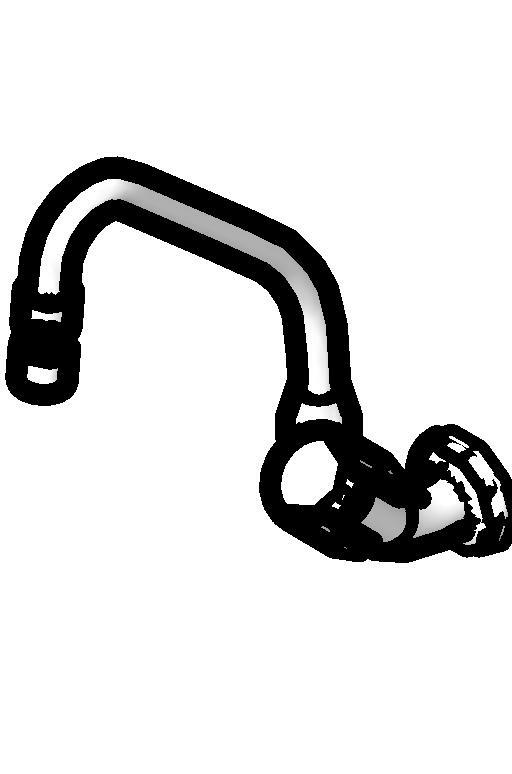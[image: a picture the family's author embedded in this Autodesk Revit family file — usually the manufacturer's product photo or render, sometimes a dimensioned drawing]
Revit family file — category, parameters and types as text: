
# Revit family: Deca_Torneira de parede para cozinha_Targa_1168.40
name_source: partatom
category: Plumbing Fixtures
units: mm (PartAtom-declared; Revit-internal decimal feet)

## family parameters
Cut with Voids When Loaded = No
Host = Face
Part Type = Normal
Room Calculation Point = No
Round Connector Dimension = Use Radius
Shared = No

## types (1)
- 1168.C40.CR_Cromado
    Acompanha o Produto = -
    Aprovado por = quattroD
    Atendimento ao Cliente = 0800-0117073
    CWFU = 0
    Categoria = METAIS PARA COZINHA
    Composição Anel Vedação = -
    Composição Assento = -
    Composição Básica = Liga de Cobre (bronze e latão),Plásticos de Engenharia,Elastômeros
    Composição Componente = -
    Consumo = -
    Cor Interna = -
    Cor Principal = Cromado
    Cor Secundária = -
    Cores Componente = -
    Criado por = quattroD
    Código Pai = 1168.40
    Default Elevation = 1100 mm
    Description = Torneira de parede para cozinha
    Diâmetro Água Fria = 15 mm  [stored 0.0492126 ft]
    HWFU = 0
    Informações Complementares = -
    Itens de Instalação = -
    Linha = Targa
    Manufacturer = Deca
    Material = Deca_Cromado
    Model = 1168.C40.CR
    Norma = NBR10281
    Peso Líquido (Kg) = 0.869
    Pressão máx. funcionamento = 40 MCA
    Pressão mín. Aquec. Acúmulo = -
    Pressão mín. Aquec. Passagem = -
    Pressão mín. funcionamento = 2 MCA
    Raio Água Fria = 8 mm  [stored 0.0262467 ft]
    Saída de Esgoto = -
    Segmento = Banheiro Competitivo
    Tipo de dispositivo economizador = Não
    Tipo de mecanismo utilizado = MVC -1/4 volta
    Tipo de rosca de entrada = BSP NBR 8133
    Tipo de rosca de saída = -
    URL = www.deca.com.br
    Vazão na Pressão máx. (L/min) = 16
    Vazão na Pressão mín. (L/min) = 4
    WFU = 0

note: source unit labels omitted for Vazão na Pressão máx. (L/min), Vazão na Pressão mín. (L/min) — the stored unit's dimension contradicts the parameter name (converter mislabeling)

note: [stored X ft] marks values corroborated as IEEE doubles in the binary element streams (Revit-internal decimal feet)

## geometry (parser evidence)
native form markers: Sweep x4
no freeform markers — native parametric forms only
